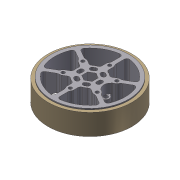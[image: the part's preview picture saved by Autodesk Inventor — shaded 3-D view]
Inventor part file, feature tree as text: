
AUTODESK INVENTOR PART (.ipt)
format: ipt  version: 2012 (Build 160160000, 160)  size: 396,288 bytes
history: native  units: in
note: dims shown in document units (in); Inventor stores cm internally (conversion verified against a paired STEP export)
features: other x2, extrude x1, imported_body x1, sketch x1
ambient origin geometry x8: Origin, YZ Plane, XZ Plane, XY Plane, X Axis, Y Axis, Z Axis, Center Point
feature tree (5):
  other  "Cut-Extrude9"
  other  "4 Perf ThruTread 500 Hex1"
  extrude  "Extrusion1"  Depth=1.0in TaperAngle=0.0deg
  imported_body  "Base1"
  sketch  "Sketch1"  dims[d0=4.0in d1=1.0in d2=0.0in]
